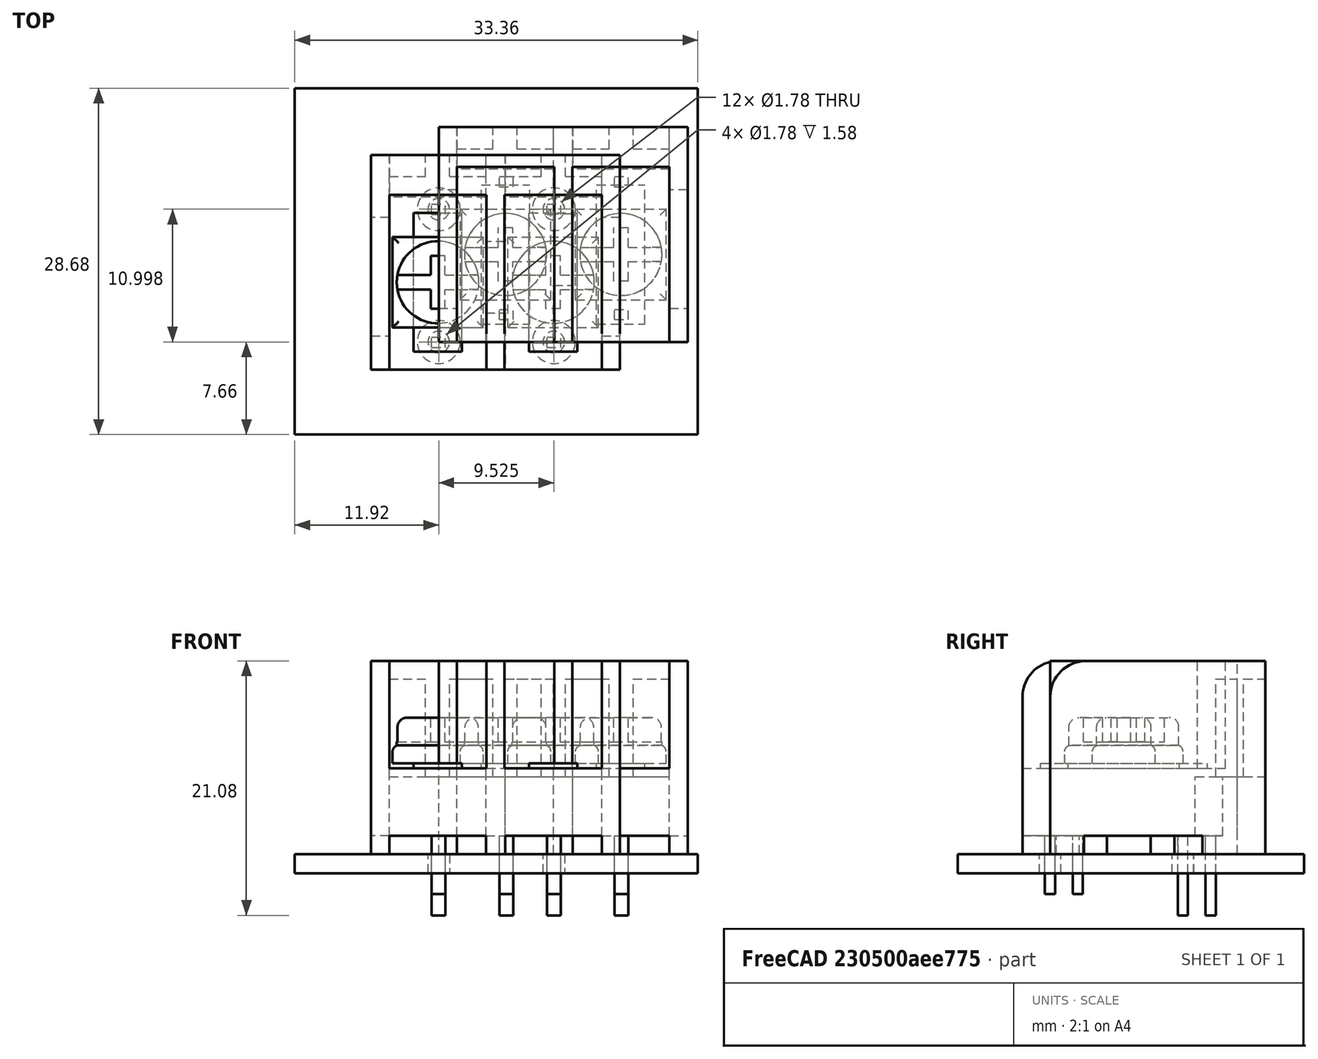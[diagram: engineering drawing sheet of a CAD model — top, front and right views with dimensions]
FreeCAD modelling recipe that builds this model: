
FCSTD DOCUMENT  (FreeCAD 0.18R16131 (Git))
Label: Barrier Block_6DBL-02-006
License: All rights reserved
LicenseURL: http://en.wikipedia.org/wiki/All_rights_reserved
objects: Part::Feature×23, Part::Box×18, Part::FeaturePython×6, PartDesign::FeatureBase×5, PartDesign::Fillet×5, PartDesign::Body×5, Part::Cut×5, Part::MultiFuse×4, App::DocumentObjectGroup×4, App::Part×2, PartDesign::Boolean×1, Part::Part2DObjectPython×1, Part::Extrusion×1
note: 74 computed .brp shape members not serialized (recipe doc carries the construction recipe); baked Part::Feature solids carry a one-line shape summary decoded from their .brp

FEATURE [Part::Box] Box001  label="Plastic Shell Screw Cutout 1"
  AttacherType = Attacher::AttachEngine3D
  Height = 8.9
  Length = 8.05
  Placement = pos=(1.5,0,7.1) rot=(0,0,1;0rad)
  Width = 14.5
FEATURE [Part::Box] Box002  label="Plastic Shell Screw Cutout 2"
  AttacherType = Attacher::AttachEngine3D
  Height = 8.9
  Length = 8.05
  Placement = pos=(11.05,0,7.1) rot=(0,0,1;0rad)
  Width = 14.5
FEATURE [PartDesign::FeatureBase] BaseFeature
FEATURE [PartDesign::Fillet] Fillet
  Base = -> BaseFeature [Edge10]
  BaseFeature = -> BaseFeature
  Radius = 3
FEATURE [PartDesign::Boolean] Boolean
  BaseFeature = -> Fillet
  Group = -> [Box002,Box001]
  Type = 1
FEATURE [PartDesign::Body] Body
  Group = -> [BaseFeature,Fillet,Boolean]
  Origin = -> Origin
  Tip = -> Boolean
FEATURE [Part::Part2DObjectPython] Wire  # Draft 2D object (typed FeaturePython)
  ChamferSize = 0
  Closed = true
  End = (-1.00865,2.80032,0)
  FilletRadius = 0
  Length = 115.066
  MakeFace = false
  Placement = pos=(1.5,2.8,0) rot=(0,0,1;0rad)
  Points = (20) [(0,0,0),(0,-3.80199,0),(8,-3.80175,0),(8,1.90004,0),(9.6,1.90018,0),(9.6,-3.8017,0),(17.6,-3.80145,0),(17.6,0.000442743,0),(20.4954,-8.88178e-16,0),+11 more]
  Start = (1.5,2.8,0)
  Subdivisions = 0
FEATURE [Part::Extrusion] Extrude
  Base = -> Wire
  Dir = (0,0,1)
  DirMode = 2
  FaceMakerClass = Part::FaceMakerBullseye
  LengthFwd = 1.5
  LengthRev = 0
  Solid = true
  Symmetric = false
FEATURE [Part::Cut] Cut
  Base = -> Body
  Tool = -> Extrude
FEATURE [Part::Box] Box003  label="Cube001"
  AttacherType = Attacher::AttachEngine3D
  Height = 6.4
  Length = 8
  Placement = pos=(1.5,14.3,0) rot=(0,0,1;0rad)
  Width = 3.5
FEATURE [Part::Box] Box004  label="Cube002"
  AttacherType = Attacher::AttachEngine3D
  Height = 8.1
  Length = 3
  Placement = pos=(1.5,16,6.4) rot=(0,0,1;0rad)
  Width = 1.8
FEATURE [Part::Box] Box005  label="Cube003"
  AttacherType = Attacher::AttachEngine3D
  Height = 8.1
  Length = 3
  Placement = pos=(6.5,16,6.4) rot=(0,0,1;0rad)
  Width = 1.8
FEATURE [Part::MultiFuse] Fusion
  Shapes = -> [Box003,Box004,Box005]
FEATURE [Part::Box] Box006  label="Cube004"
  AttacherType = Attacher::AttachEngine3D
  Height = 6.4
  Length = 8
  Placement = pos=(1.5,14.3,0) rot=(0,0,1;0rad)
  Width = 3.5
FEATURE [Part::Box] Box007  label="Cube005"
  AttacherType = Attacher::AttachEngine3D
  Height = 8.1
  Length = 3
  Placement = pos=(1.5,16,6.4) rot=(0,0,1;0rad)
  Width = 1.8
FEATURE [Part::Box] Box008  label="Cube006"
  AttacherType = Attacher::AttachEngine3D
  Height = 8.1
  Length = 3
  Placement = pos=(6.5,16,6.4) rot=(0,0,1;0rad)
  Width = 1.8
FEATURE [Part::MultiFuse] Fusion001
  Placement = pos=(9.6,0,0) rot=(0,0,1;0rad)
  Shapes = -> [Box006,Box007,Box008]
FEATURE [Part::Cut] Cut001
  Base = -> Cut
  Tool = -> Fusion
FEATURE [Part::Cut] Cut002  label="Plastic Body"
  Base = -> Cut001
  Tool = -> Fusion001
FEATURE [Part::Box] Box  label="Pin 1"
  AttacherType = Attacher::AttachEngine3D
  Height = 4.8
  Length = 1.14
  Placement = pos=(5.02,1.86,-3.3) rot=(0,0,1;0rad)
  Width = 0.85
FEATURE [Part::Box] Box009  label="Pin 2"
  AttacherType = Attacher::AttachEngine3D
  Height = 4.8
  Length = 1.14
  Placement = pos=(14.55,1.86,-3.3) rot=(0,0,1;0rad)
  Width = 0.85
FEATURE [Part::Box] Box010  label="Pin 3"
  AttacherType = Attacher::AttachEngine3D
  Height = 6.58
  Length = 1.14
  Placement = pos=(5.02,12.86,-5.08) rot=(0,0,1;0rad)
  Width = 0.85
FEATURE [Part::Box] Box011  label="Pin 4"
  AttacherType = Attacher::AttachEngine3D
  Height = 6.58
  Length = 1.14
  Placement = pos=(14.55,12.86,-5.08) rot=(0,0,1;0rad)
  Width = 0.85
FEATURE [Part::Box] Box012  label="Strip"
  AttacherType = Attacher::AttachEngine3D
  Height = 0.4
  Length = 4
  Placement = pos=(3.525,1.5,7.1) rot=(0,0,1;0rad)
  Width = 11.5
FEATURE [App::DocumentObjectGroup] Group  label="Pins"
  Group = -> [Box,Box009,Box010,Box011]
FEATURE [PartDesign::FeatureBase] BaseFeature001
FEATURE [PartDesign::Fillet] Fillet001
  Base = -> BaseFeature001 [Face6]
  BaseFeature = -> BaseFeature001
  Radius = 0.5
FEATURE [PartDesign::Body] Body001  label="Spacer"
  Group = -> [BaseFeature001,Fillet001]
  Origin = -> Origin001
  Placement = pos=(1.775,3.5,7.5) rot=(0,0,1;0rad)
  Tip = -> Fillet001
FEATURE [PartDesign::FeatureBase] BaseFeature002
FEATURE [PartDesign::Fillet] Fillet002
  Base = -> BaseFeature002 [Face2]
  BaseFeature = -> BaseFeature002
  Radius = 0.8
FEATURE [PartDesign::Body] Body002
  Group = -> [BaseFeature002,Fillet002]
  Origin = -> Origin002
  Tip = -> Fillet002
FEATURE [Part::Box] Box014  label="Cube"
  AttacherType = Attacher::AttachEngine3D
  Height = 2
  Length = 7
  Placement = pos=(-3.5,-0.6,0.3) rot=(0,0,1;0rad)
  Width = 1.2
FEATURE [Part::Box] Box015  label="Cube008"
  AttacherType = Attacher::AttachEngine3D
  Height = 2
  Length = 4.4
  Placement = pos=(0.6,-2.2,0.3) rot=(0,0,1;1.5708rad)
  Width = 1.2
FEATURE [Part::MultiFuse] Fusion002
  Shapes = -> [Box014,Box015]
FEATURE [Part::Cut] Cut003
  Base = -> Body002
  Placement = pos=(5.525,7.25,9) rot=(0,0,1;0rad)
  Tool = -> Fusion002
FEATURE [App::DocumentObjectGroup] Group001  label="Terminal Strip"
  Group = -> [Box012,Body001,Cut003]
FEATURE [Part::Box] Box016  label="Strip001"
  AttacherType = Attacher::AttachEngine3D
  Height = 0.4
  Length = 4
  Placement = pos=(13.07,1.5,7.1) rot=(0,0,1;0rad)
  Width = 11.5
FEATURE [Part::Box] Box018  label="Cube010"
  AttacherType = Attacher::AttachEngine3D
  Height = 2
  Length = 7
  Placement = pos=(-3.5,-0.6,0.3) rot=(0,0,1;0rad)
  Width = 1.2
FEATURE [Part::Box] Box019  label="Cube011"
  AttacherType = Attacher::AttachEngine3D
  Height = 2
  Length = 4.4
  Placement = pos=(0.6,-2.2,0.3) rot=(0,0,1;1.5708rad)
  Width = 1.2
FEATURE [Part::MultiFuse] Fusion003
  Shapes = -> [Box018,Box019]
FEATURE [PartDesign::FeatureBase] BaseFeature003
FEATURE [PartDesign::Fillet] Fillet004
  Base = -> BaseFeature003 [Face6]
  BaseFeature = -> BaseFeature003
  Radius = 0.5
FEATURE [PartDesign::Body] Body003  label="Spacer001"
  Group = -> [BaseFeature003,Fillet004]
  Origin = -> Origin003
  Placement = pos=(11.32,3.5,7.5) rot=(0,0,1;0rad)
  Tip = -> Fillet004
FEATURE [PartDesign::FeatureBase] BaseFeature004
FEATURE [PartDesign::Fillet] Fillet003
  Base = -> BaseFeature004 [Face2]
  BaseFeature = -> BaseFeature004
  Radius = 0.8
FEATURE [PartDesign::Body] Body004
  Group = -> [BaseFeature004,Fillet003]
  Origin = -> Origin004
  Tip = -> Fillet003
FEATURE [Part::Cut] Cut004
  Base = -> Body004
  Placement = pos=(15.08,7.25,9) rot=(0,0,1;0rad)
  Tool = -> Fusion003
FEATURE [App::DocumentObjectGroup] Group002  label="Terminal Strip001"
  Group = -> [Box016,Body003,Cut004]
FEATURE [App::Part] Part  label="Barrier Block_6DBL-02-006"
  Group = -> [Fusion001,Fusion,Box004,Box008,Box005,Box003,Box007,Box006,Wire,Body,Extrude,Cut001,Cut,Cut002,Box009,Box010,Box,Box011,Group,Box012,Cut003,Fusion002,Box014,Box015,Body001,Body002,Group001,Cut004,Box016,Fusion003,Body004,Body003,Box018,Box019,Group002]
  Origin = -> Origin005
  Placement = pos=(-5.6,-2.3,0) rot=(0,0,1;0rad)
FEATURE [Part::FeaturePython] FCrtYd_lines  label="FCrtYd"  # a2plus imported part (geometry in sourceFile) (typed FeaturePython)
  fixedPosition = true
FEATURE [Part::FeaturePython] Filk_lines  label="FrontSilk"  # a2plus imported part (geometry in sourceFile) (typed FeaturePython)
  fixedPosition = true
FEATURE [Part::FeaturePython] TopPads  # a2plus imported part (geometry in sourceFile) (typed FeaturePython)
  fixedPosition = true
FEATURE [Part::FeaturePython] BotPads  # a2plus imported part (geometry in sourceFile) (typed FeaturePython)
  fixedPosition = true
FEATURE [Part::FeaturePython] THPs  label="PTHs"  # a2plus imported part (geometry in sourceFile) (typed FeaturePython)
  fixedPosition = true
FEATURE [Part::FeaturePython] newPCB  label="Pcb"  # a2plus imported part (geometry in sourceFile) (typed FeaturePython)
  fixedPosition = true
FEATURE [App::DocumentObjectGroup] BarrierBlock_TE_1x02_P0_375in_6DBL_02_006_fp
  Group = -> [FCrtYd_lines,Filk_lines,TopPads,BotPads,THPs,newPCB]
FEATURE [Part::Feature] Cut002_cp  label="Plastic Body_cp"
  shape: bbox 20.6 x 17.8 x 16 mm, 63 faces (baked)
FEATURE [Part::Feature] Box009_cp  label="Pin 2_cp"
  Placement = pos=(14.55,1.86,-3.3) rot=(0,0,1;0rad)
  shape: bbox 1.14 x 0.85 x 4.8 mm, 6 faces (baked)
FEATURE [Part::Feature] Box010_cp  label="Pin 3_cp"
  Placement = pos=(5.02,12.86,-5.08) rot=(0,0,1;0rad)
  shape: bbox 1.14 x 0.85 x 6.58 mm, 6 faces (baked)
FEATURE [Part::Feature] Box_cp  label="Pin 1_cp"
  Placement = pos=(5.02,1.86,-3.3) rot=(0,0,1;0rad)
  shape: bbox 1.14 x 0.85 x 4.8 mm, 6 faces (baked)
FEATURE [Part::Feature] Box011_cp  label="Pin 4_cp"
  Placement = pos=(14.55,12.86,-5.08) rot=(0,0,1;0rad)
  shape: bbox 1.14 x 0.85 x 6.58 mm, 6 faces (baked)
FEATURE [Part::Feature] Box012_cp  label="Strip_cp"
  Placement = pos=(3.525,1.5,7.1) rot=(0,0,1;0rad)
  shape: bbox 4 x 11.5 x 0.4 mm, 6 faces (baked)
FEATURE [Part::Feature] Cut003_cp
  Placement = pos=(5.525,7.25,9) rot=(0,0,1;0rad)
  shape: bbox 7.245 x 7.36 x 2.3 mm, 21 faces (baked)
FEATURE [Part::Feature] Fillet001_cp
  Placement = pos=(1.775,3.5,7.5) rot=(0,0,1;0rad)
  shape: bbox 7.5 x 7.5 x 1.5 mm, 10 faces (baked)
FEATURE [Part::Feature] Cut004_cp
  Placement = pos=(15.08,7.25,9) rot=(0,0,1;0rad)
  shape: bbox 7.245 x 7.36 x 2.3 mm, 21 faces (baked)
FEATURE [Part::Feature] Box016_cp  label="Strip001_cp"
  Placement = pos=(13.07,1.5,7.1) rot=(0,0,1;0rad)
  shape: bbox 4 x 11.5 x 0.4 mm, 6 faces (baked)
FEATURE [Part::Feature] Fillet004_cp
  Placement = pos=(11.32,3.5,7.5) rot=(0,0,1;0rad)
  shape: bbox 7.5 x 7.5 x 1.5 mm, 10 faces (baked)
FEATURE [App::Part] Part001  label="Barrier Block_6DBL-02-006 - Revised"
  Group = -> [Cut002_cp,Box009_cp,Box010_cp,Box_cp,Box011_cp,Box012_cp,Cut003_cp,Fillet001_cp,Cut004_cp,Box016_cp,Fillet004_cp]
  Origin = -> Origin006
  Placement = pos=(-5.6,-2.3,0) rot=(0,0,1;0rad)
FEATURE [Part::Feature] Cut002_cp_cp  label="Plastic Body_cp_cp"
  Placement = pos=(-5.6,-2.3,0) rot=(0,0,1;0rad)
  shape: bbox 20.6 x 17.8 x 16 mm, 63 faces (baked)
FEATURE [Part::Feature] Box009_cp_cp  label="Pin 2_cp_cp"
  Placement = pos=(8.95,-0.44,-3.3) rot=(0,0,1;0rad)
  shape: bbox 1.14 x 0.85 x 4.8 mm, 6 faces (baked)
FEATURE [Part::Feature] Box010_cp_cp  label="Pin 3_cp_cp"
  Placement = pos=(-0.58,10.56,-5.08) rot=(0,0,1;0rad)
  shape: bbox 1.14 x 0.85 x 6.58 mm, 6 faces (baked)
FEATURE [Part::Feature] Box_cp_cp  label="Pin 1_cp_cp"
  Placement = pos=(-0.58,-0.44,-3.3) rot=(0,0,1;0rad)
  shape: bbox 1.14 x 0.85 x 4.8 mm, 6 faces (baked)
FEATURE [Part::Feature] Box011_cp_cp  label="Pin 4_cp_cp"
  Placement = pos=(8.95,10.56,-5.08) rot=(0,0,1;0rad)
  shape: bbox 1.14 x 0.85 x 6.58 mm, 6 faces (baked)
FEATURE [Part::Feature] Box012_cp_cp  label="Strip_cp_cp"
  Placement = pos=(-2.075,-0.8,7.1) rot=(0,0,1;0rad)
  shape: bbox 4 x 11.5 x 0.4 mm, 6 faces (baked)
FEATURE [Part::Feature] Cut003_cp_cp
  Placement = pos=(-0.075,4.95,9) rot=(0,0,1;0rad)
  shape: bbox 7.245 x 7.36 x 2.3 mm, 21 faces (baked)
FEATURE [Part::Feature] Fillet001_cp_cp
  Placement = pos=(-3.825,1.2,7.5) rot=(0,0,1;0rad)
  shape: bbox 7.5 x 7.5 x 1.5 mm, 10 faces (baked)
FEATURE [Part::Feature] Cut004_cp_cp
  Placement = pos=(9.48,4.95,9) rot=(0,0,1;0rad)
  shape: bbox 7.245 x 7.36 x 2.3 mm, 21 faces (baked)
FEATURE [Part::Feature] Box016_cp_cp  label="Strip001_cp_cp"
  Placement = pos=(7.47,-0.8,7.1) rot=(0,0,1;0rad)
  shape: bbox 4 x 11.5 x 0.4 mm, 6 faces (baked)
FEATURE [Part::Feature] Fillet004_cp_cp
  Placement = pos=(5.72,1.2,7.5) rot=(0,0,1;0rad)
  shape: bbox 7.5 x 7.5 x 1.5 mm, 10 faces (baked)
FEATURE [Part::Feature] Shape  label="Barrier_Block_6DBL_02_006___Revised_cp"
  shape: bbox 20.6 x 17.8 x 21.08 mm, 161 faces, 11 solids (baked)
